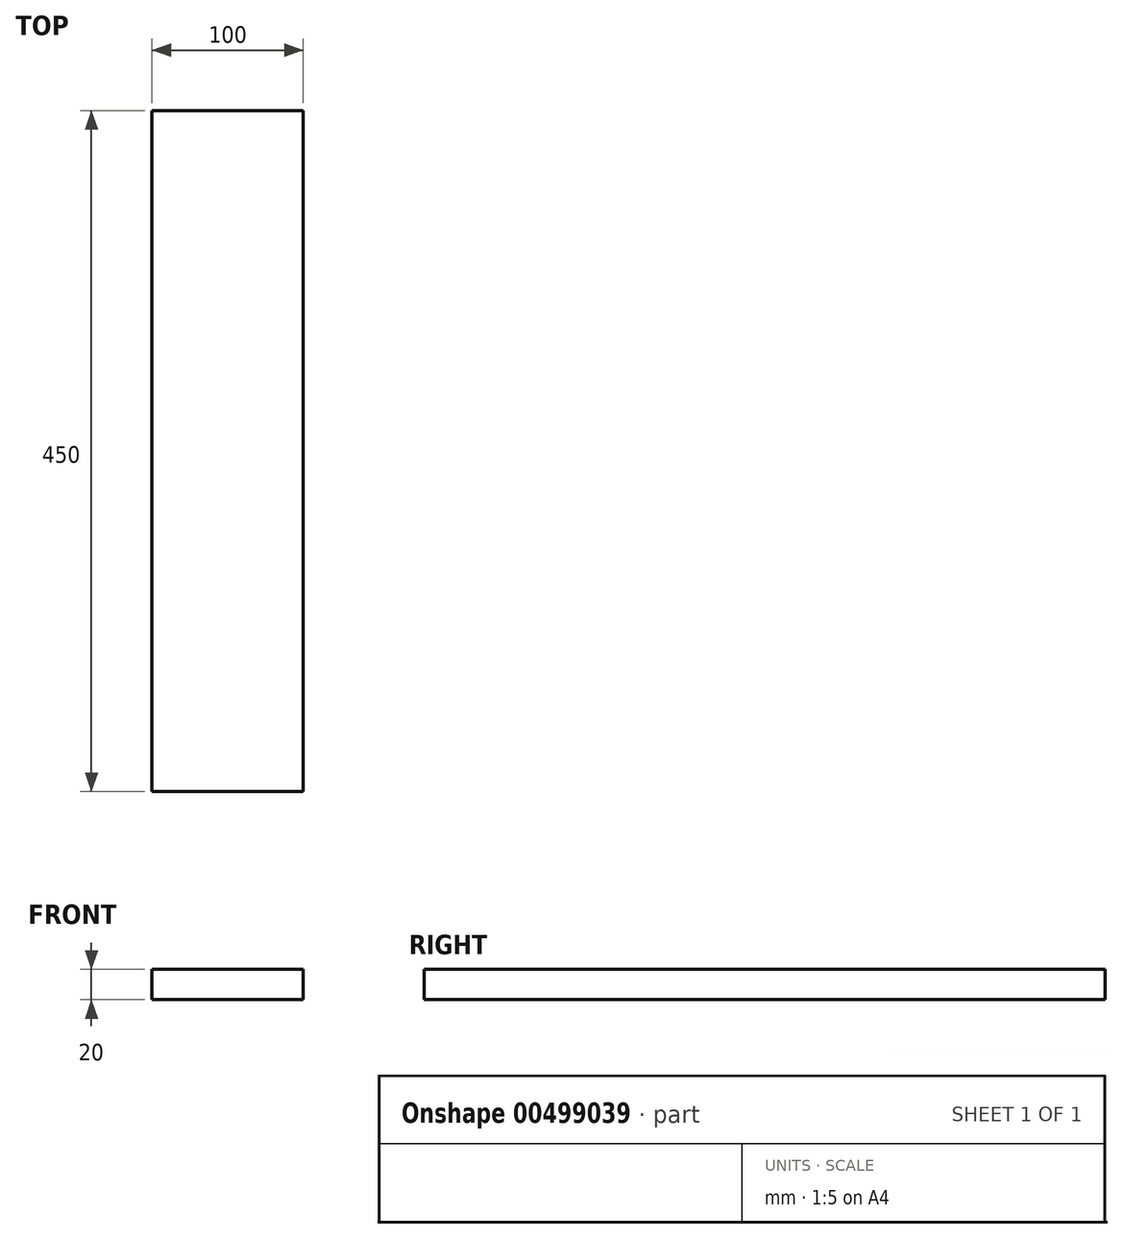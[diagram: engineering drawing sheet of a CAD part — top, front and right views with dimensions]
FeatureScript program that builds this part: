
annotation { "Feature Type Name" : "Feature", "Feature Type Description" : "" }
export const myFeature = defineFeature(function(context is Context, id is Id, definition is map)
    precondition{}
    {
        {
            var Q0;
            Q0=qCreatedBy(makeId("Top.planeOp"),FACE);
            var sketch = newSketch(context, id + "F0", { "sketchPlane" : qUnion([Q0])});
            skLineSegment(sketch, "E0.bottom", {"start": v(-68.86, 260.14) * mm, "end": v(31.14, 260.14) * mm});
            skLineSegment(sketch, "E0.top", {"start": v(-68.86, -189.86) * mm, "end": v(31.14, -189.86) * mm});
            skLineSegment(sketch, "E0.left", {"start": v(-68.86, 260.14) * mm, "end": v(-68.86, -189.86) * mm});
            skLineSegment(sketch, "E0.right", {"start": v(31.14, 260.14) * mm, "end": v(31.14, -189.86) * mm});
            skSolve(sketch);
        }
        {
            var Q0;
            Q0 = qSketchRegion(id + "F0", true);
            extrude(context, id + "F1", {"entities" : qUnion([Q0]), "depth" : 20 * mm, "offsetDistance" : 25 * mm});
        }
    });
